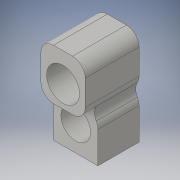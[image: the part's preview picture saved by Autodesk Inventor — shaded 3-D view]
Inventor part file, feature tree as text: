
AUTODESK INVENTOR PART (.ipt)
format: ipt  version: 2016 (Build 200138000, 138)  size: 184,832 bytes
history: native  units: mm
features: sketch x6, extrude x4, fillet x3, other x1, projected_geometry x1
ambient origin geometry x8: Origin, YZ Plane, XZ Plane, XY Plane, X Axis, Y Axis, Z Axis, Center Point
bodies: Body1 (feature_tree)
feature tree (15):
  other  "ソリッド1"
  extrude  "押し出し1"  Depth=7.0mm
  extrude  "押し出し2"  Depth=8.5mm
  fillet  "フィレット1"  Radius=15.0mm
  fillet  "フィレット2"  Radius=4.7mm
  sketch  "スケッチ4"
  extrude  "押し出し4"  Depth=4.0mm
  extrude  "押し出し5"  Depth=3.5mm
  fillet  "フィレット3"  Radius=5.2mm
  sketch  "スケッチ9"
  sketch  "スケッチ1"
  sketch  "スケッチ2"
  sketch  "スケッチ6"
  sketch  "スケッチ8"
  projected_geometry  "投影ループ1"
